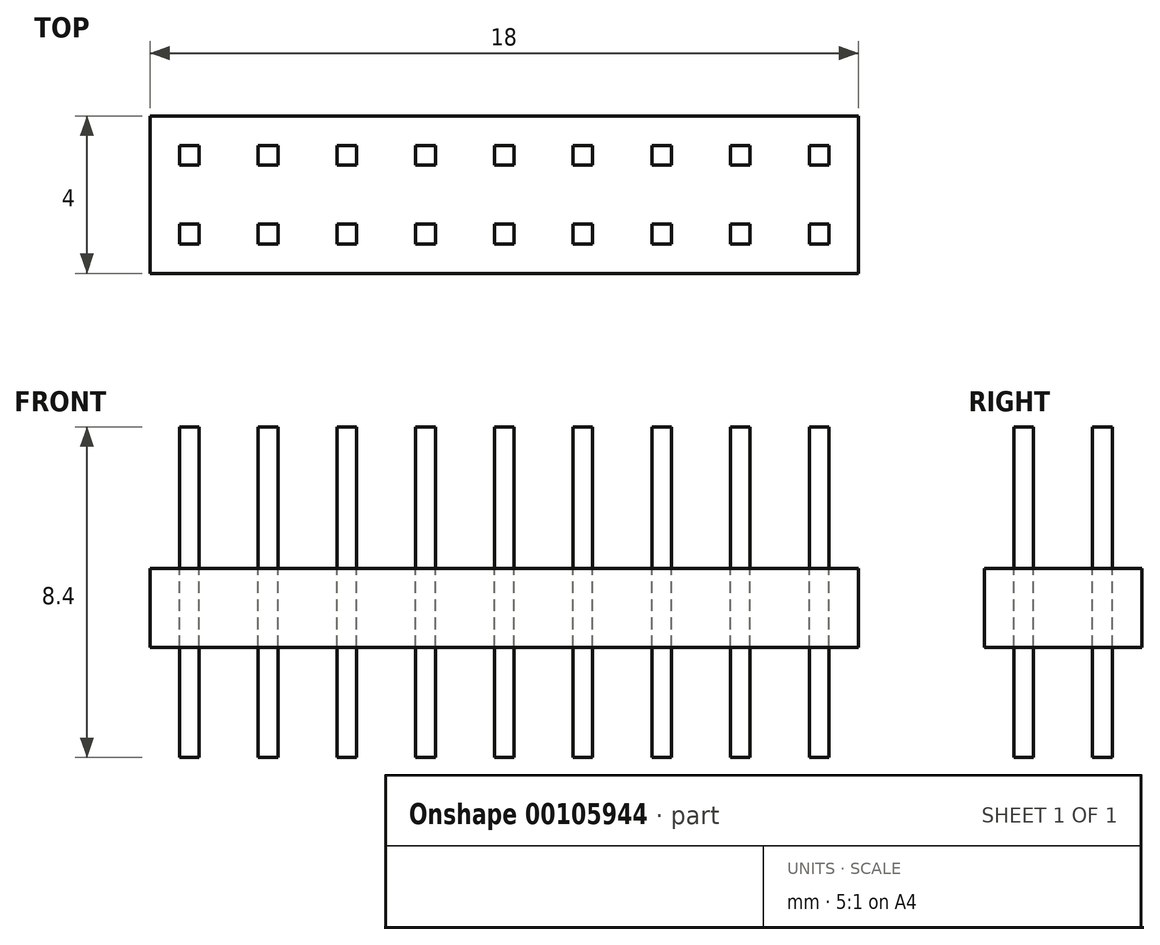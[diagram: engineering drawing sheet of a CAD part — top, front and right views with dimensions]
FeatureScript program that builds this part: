
annotation { "Feature Type Name" : "Feature", "Feature Type Description" : "" }
export const myFeature = defineFeature(function(context is Context, id is Id, definition is map)
    precondition{}
    {
        {
            var Q0;
            Q0=qCreatedBy(makeId("Top.planeOp"),FACE);
            var sketch = newSketch(context, id + "F0", { "sketchPlane" : qUnion([Q0])});
            skLineSegment(sketch, "E0.bottom", {"start": v(-9, 2) * mm, "end": v(9, 2) * mm});
            skLineSegment(sketch, "E0.top", {"start": v(-9, -2) * mm, "end": v(9, -2) * mm});
            skLineSegment(sketch, "E0.left", {"start": v(-9, 2) * mm, "end": v(-9, -2) * mm});
            skLineSegment(sketch, "E0.right", {"start": v(9, 2) * mm, "end": v(9, -2) * mm});
            skSolve(sketch);
        }
        {
            var Q0;
            Q0 = qSketchRegion(id + "F0", true);
            extrude(context, id + "F1", {"entities" : qUnion([Q0]), "depth" : 2 * mm});
        }
        {
            var Q0;
            Q0=makeQuery(id+"F1.opExtrude","CAP_FACE",FACE,{"disambiguationData":[OSD([sQuery(id+"F0.wireOp",EDGE,"E0.bottom"),sQuery(id+"F0.wireOp",EDGE,"E0.top"),sQuery(id+"F0.wireOp",EDGE,"E0.left"),sQuery(id+"F0.wireOp",EDGE,"E0.right")])],"isStart":false});
            var sketch = newSketch(context, id + "F2", { "sketchPlane" : qUnion([Q0])});
            skLineSegment(sketch, "E1.bottom", {"start": v(-0.25, 1.25) * mm, "end": v(0.25, 1.25) * mm});
            skLineSegment(sketch, "E1.top", {"start": v(-0.25, 0.75) * mm, "end": v(0.25, 0.75) * mm});
            skLineSegment(sketch, "E1.left", {"start": v(-0.25, 1.25) * mm, "end": v(-0.25, 0.75) * mm});
            skLineSegment(sketch, "E1.right", {"start": v(0.25, 1.25) * mm, "end": v(0.25, 0.75) * mm});
            skLineSegment(sketch, "E2.MirrorCS", {"start": v(-0.25, -1.25) * mm, "end": v(0.25, -1.25) * mm});
            skLineSegment(sketch, "E3.MirrorCS", {"start": v(-0.25, -0.75) * mm, "end": v(0.25, -0.75) * mm});
            skLineSegment(sketch, "E4.MirrorCS", {"start": v(-0.25, -1.25) * mm, "end": v(-0.25, -0.75) * mm});
            skLineSegment(sketch, "E5.MirrorCS", {"start": v(0.25, -1.25) * mm, "end": v(0.25, -0.75) * mm});
            skLineSegment(sketch, "E6.MirrorCS", {"start": v(-1.75, -1.25) * mm, "end": v(-1.75, -0.75) * mm});
            skLineSegment(sketch, "E7.MirrorCS", {"start": v(-1.75, -0.75) * mm, "end": v(-2.25, -0.75) * mm});
            skLineSegment(sketch, "E8.MirrorCS", {"start": v(-2.25, -1.25) * mm, "end": v(-2.25, -0.75) * mm});
            skLineSegment(sketch, "E9.MirrorCS", {"start": v(-1.75, -1.25) * mm, "end": v(-2.25, -1.25) * mm});
            skLineSegment(sketch, "E10.MirrorCS", {"start": v(-2.25, 1.25) * mm, "end": v(-2.25, 0.75) * mm});
            skLineSegment(sketch, "E11.MirrorCS", {"start": v(-1.75, 1.25) * mm, "end": v(-1.75, 0.75) * mm});
            skLineSegment(sketch, "E12.MirrorCS", {"start": v(-1.75, 1.25) * mm, "end": v(-2.25, 1.25) * mm});
            skLineSegment(sketch, "E13.MirrorCS", {"start": v(-1.75, 0.75) * mm, "end": v(-2.25, 0.75) * mm});
            skLineSegment(sketch, "E14.MirrorCS", {"start": v(-4.25, -1.25) * mm, "end": v(-4.25, -0.75) * mm});
            skLineSegment(sketch, "E15.MirrorCS", {"start": v(-4.25, -0.75) * mm, "end": v(-3.75, -0.75) * mm});
            skLineSegment(sketch, "E16.MirrorCS", {"start": v(-4.25, 0.75) * mm, "end": v(-3.75, 0.75) * mm});
            skLineSegment(sketch, "E17.MirrorCS", {"start": v(-4.25, 1.25) * mm, "end": v(-4.25, 0.75) * mm});
            skLineSegment(sketch, "E18.MirrorCS", {"start": v(-4.25, 1.25) * mm, "end": v(-3.75, 1.25) * mm});
            skLineSegment(sketch, "E19.MirrorCS", {"start": v(-3.75, 1.25) * mm, "end": v(-3.75, 0.75) * mm});
            skLineSegment(sketch, "E20.MirrorCS", {"start": v(-4.25, -1.25) * mm, "end": v(-3.75, -1.25) * mm});
            skLineSegment(sketch, "E21.MirrorCS", {"start": v(-3.75, -1.25) * mm, "end": v(-3.75, -0.75) * mm});
            skLineSegment(sketch, "E22.MirrorCS", {"start": v(-5.75, -1.25) * mm, "end": v(-6.25, -1.25) * mm});
            skLineSegment(sketch, "E23.MirrorCS", {"start": v(-5.75, 0.75) * mm, "end": v(-6.25, 0.75) * mm});
            skLineSegment(sketch, "E24.MirrorCS", {"start": v(-5.75, -0.75) * mm, "end": v(-6.25, -0.75) * mm});
            skLineSegment(sketch, "E25.MirrorCS", {"start": v(-5.75, 1.25) * mm, "end": v(-6.25, 1.25) * mm});
            skLineSegment(sketch, "E26.MirrorCS", {"start": v(-6.25, 1.25) * mm, "end": v(-6.25, 0.75) * mm});
            skLineSegment(sketch, "E27.MirrorCS", {"start": v(-5.75, -1.25) * mm, "end": v(-5.75, -0.75) * mm});
            skLineSegment(sketch, "E28.MirrorCS", {"start": v(-6.25, -1.25) * mm, "end": v(-6.25, -0.75) * mm});
            skLineSegment(sketch, "E29.MirrorCS", {"start": v(-5.75, 1.25) * mm, "end": v(-5.75, 0.75) * mm});
            skLineSegment(sketch, "E30.MirrorCS", {"start": v(-8.25, 0.75) * mm, "end": v(-7.75, 0.75) * mm});
            skLineSegment(sketch, "E31.MirrorCS", {"start": v(-7.75, 1.25) * mm, "end": v(-7.75, 0.75) * mm});
            skLineSegment(sketch, "E32.MirrorCS", {"start": v(-8.25, 1.25) * mm, "end": v(-8.25, 0.75) * mm});
            skLineSegment(sketch, "E33.MirrorCS", {"start": v(-7.75, -1.25) * mm, "end": v(-7.75, -0.75) * mm});
            skLineSegment(sketch, "E34.MirrorCS", {"start": v(-8.25, 1.25) * mm, "end": v(-7.75, 1.25) * mm});
            skLineSegment(sketch, "E35.MirrorCS", {"start": v(-8.25, -1.25) * mm, "end": v(-8.25, -0.75) * mm});
            skLineSegment(sketch, "E36.MirrorCS", {"start": v(-8.25, -1.25) * mm, "end": v(-7.75, -1.25) * mm});
            skLineSegment(sketch, "E37.MirrorCS", {"start": v(-8.25, -0.75) * mm, "end": v(-7.75, -0.75) * mm});
            skLineSegment(sketch, "E38.MirrorCS", {"start": v(8.25, 1.25) * mm, "end": v(7.75, 1.25) * mm});
            skLineSegment(sketch, "E39.MirrorCS", {"start": v(5.75, -1.25) * mm, "end": v(5.75, -0.75) * mm});
            skLineSegment(sketch, "E40.MirrorCS", {"start": v(4.25, 1.25) * mm, "end": v(3.75, 1.25) * mm});
            skLineSegment(sketch, "E41.MirrorCS", {"start": v(8.25, 0.75) * mm, "end": v(7.75, 0.75) * mm});
            skLineSegment(sketch, "E42.MirrorCS", {"start": v(4.25, -1.25) * mm, "end": v(4.25, -0.75) * mm});
            skLineSegment(sketch, "E43.MirrorCS", {"start": v(5.75, 1.25) * mm, "end": v(6.25, 1.25) * mm});
            skLineSegment(sketch, "E44.MirrorCS", {"start": v(6.25, 1.25) * mm, "end": v(6.25, 0.75) * mm});
            skLineSegment(sketch, "E45.MirrorCS", {"start": v(5.75, -1.25) * mm, "end": v(6.25, -1.25) * mm});
            skLineSegment(sketch, "E46.MirrorCS", {"start": v(8.25, -1.25) * mm, "end": v(8.25, -0.75) * mm});
            skLineSegment(sketch, "E47.MirrorCS", {"start": v(6.25, -1.25) * mm, "end": v(6.25, -0.75) * mm});
            skLineSegment(sketch, "E48.MirrorCS", {"start": v(7.75, 1.25) * mm, "end": v(7.75, 0.75) * mm});
            skLineSegment(sketch, "E49.MirrorCS", {"start": v(3.75, 1.25) * mm, "end": v(3.75, 0.75) * mm});
            skLineSegment(sketch, "E50.MirrorCS", {"start": v(4.25, -0.75) * mm, "end": v(3.75, -0.75) * mm});
            skLineSegment(sketch, "E51.MirrorCS", {"start": v(4.25, 1.25) * mm, "end": v(4.25, 0.75) * mm});
            skLineSegment(sketch, "E52.MirrorCS", {"start": v(7.75, -1.25) * mm, "end": v(7.75, -0.75) * mm});
            skLineSegment(sketch, "E53.MirrorCS", {"start": v(5.75, -0.75) * mm, "end": v(6.25, -0.75) * mm});
            skLineSegment(sketch, "E54.MirrorCS", {"start": v(1.75, 0.75) * mm, "end": v(2.25, 0.75) * mm});
            skLineSegment(sketch, "E55.MirrorCS", {"start": v(8.25, -0.75) * mm, "end": v(7.75, -0.75) * mm});
            skLineSegment(sketch, "E56.MirrorCS", {"start": v(1.75, 1.25) * mm, "end": v(2.25, 1.25) * mm});
            skLineSegment(sketch, "E57.MirrorCS", {"start": v(4.25, 0.75) * mm, "end": v(3.75, 0.75) * mm});
            skLineSegment(sketch, "E58.MirrorCS", {"start": v(8.25, 1.25) * mm, "end": v(8.25, 0.75) * mm});
            skLineSegment(sketch, "E59.MirrorCS", {"start": v(1.75, -1.25) * mm, "end": v(1.75, -0.75) * mm});
            skLineSegment(sketch, "E60.MirrorCS", {"start": v(3.75, -1.25) * mm, "end": v(3.75, -0.75) * mm});
            skLineSegment(sketch, "E61.MirrorCS", {"start": v(1.75, -0.75) * mm, "end": v(2.25, -0.75) * mm});
            skLineSegment(sketch, "E62.MirrorCS", {"start": v(2.25, -1.25) * mm, "end": v(2.25, -0.75) * mm});
            skLineSegment(sketch, "E63.MirrorCS", {"start": v(1.75, 1.25) * mm, "end": v(1.75, 0.75) * mm});
            skLineSegment(sketch, "E64.MirrorCS", {"start": v(2.25, 1.25) * mm, "end": v(2.25, 0.75) * mm});
            skLineSegment(sketch, "E65.MirrorCS", {"start": v(4.25, -1.25) * mm, "end": v(3.75, -1.25) * mm});
            skLineSegment(sketch, "E66.MirrorCS", {"start": v(8.25, -1.25) * mm, "end": v(7.75, -1.25) * mm});
            skLineSegment(sketch, "E67.MirrorCS", {"start": v(5.75, 0.75) * mm, "end": v(6.25, 0.75) * mm});
            skLineSegment(sketch, "E68.MirrorCS", {"start": v(1.75, -1.25) * mm, "end": v(2.25, -1.25) * mm});
            skLineSegment(sketch, "E69.MirrorCS", {"start": v(5.75, 1.25) * mm, "end": v(5.75, 0.75) * mm});
            skSolve(sketch);
        }
        {
            var Q0;
            Q0 = qSketchRegion(id + "F2", true);
            extrude(context, id + "F3", {"entities" : qUnion([Q0]), "depth" : 3.6 * mm});
        }
        {
            var Q0;
            Q0 = qSketchRegion(id + "F2", true);
            extrude(context, id + "F4", {"entities" : qUnion([Q0]), "oppositeDirection" : true, "depth" : 4.8 * mm});
        }
    });
